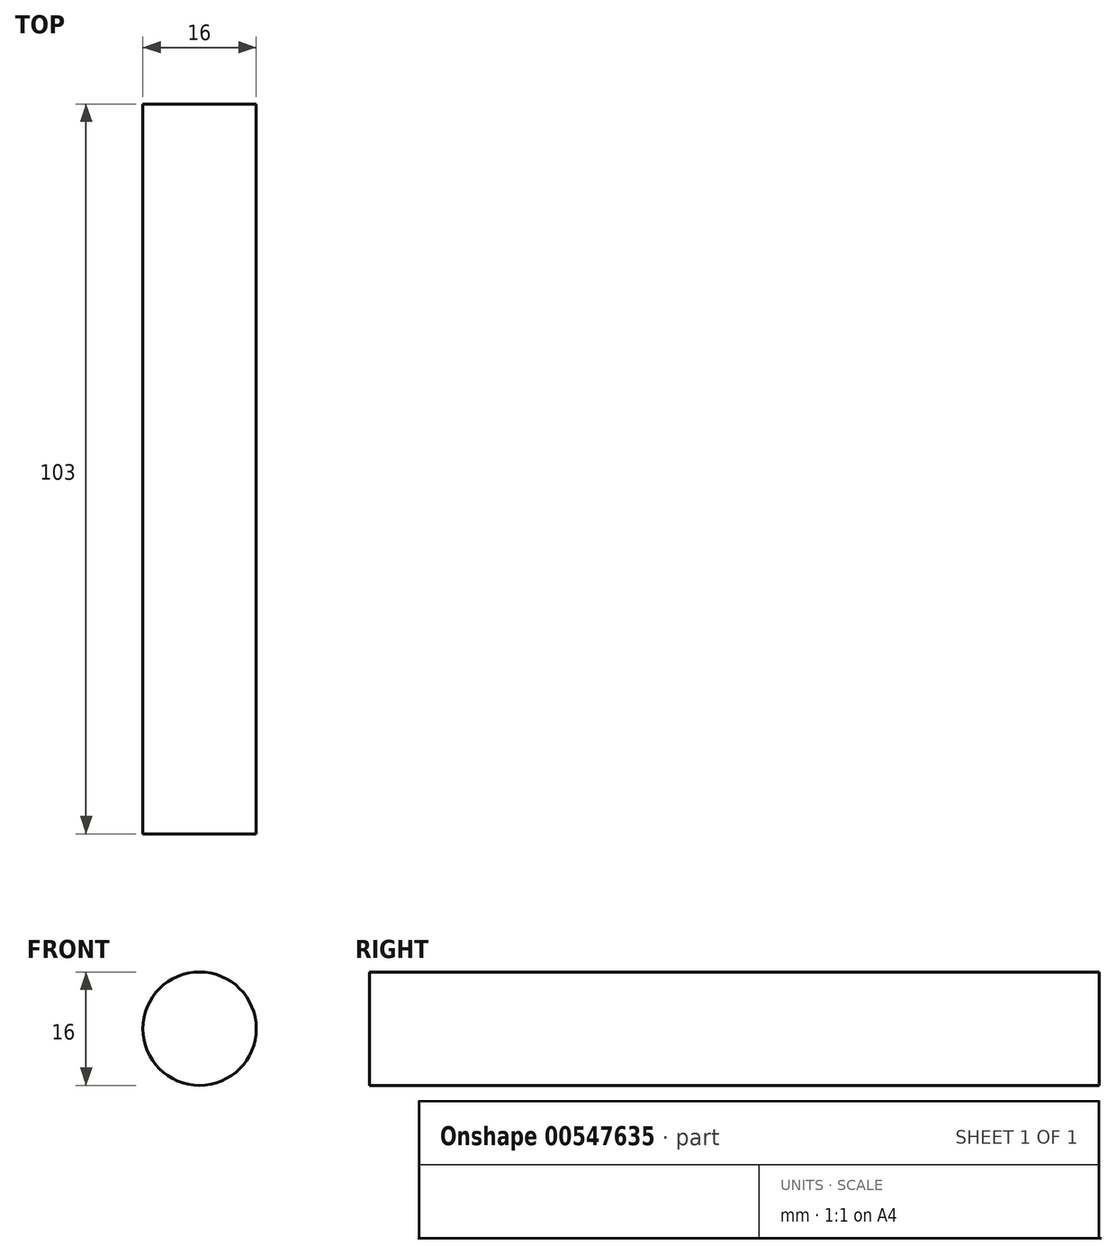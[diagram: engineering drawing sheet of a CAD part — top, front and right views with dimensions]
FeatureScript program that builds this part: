
annotation { "Feature Type Name" : "Feature", "Feature Type Description" : "" }
export const myFeature = defineFeature(function(context is Context, id is Id, definition is map)
    precondition{}
    {
        {
            var Q0;
            Q0=qCreatedBy(makeId("Front.planeOp"),FACE);
            var sketch = newSketch(context, id + "F0", { "sketchPlane" : qUnion([Q0])});
            skCircle(sketch, "E0", {"center": v(0, 0) * mm, "radius": 8 * mm});
            skSolve(sketch);
        }
        {
            var Q0;
            Q0 = qSketchRegion(id + "F0", true);
            extrude(context, id + "F1", {"entities" : qUnion([Q0]), "depth" : 103 * mm, "offsetDistance" : 25 * mm});
        }
    });
